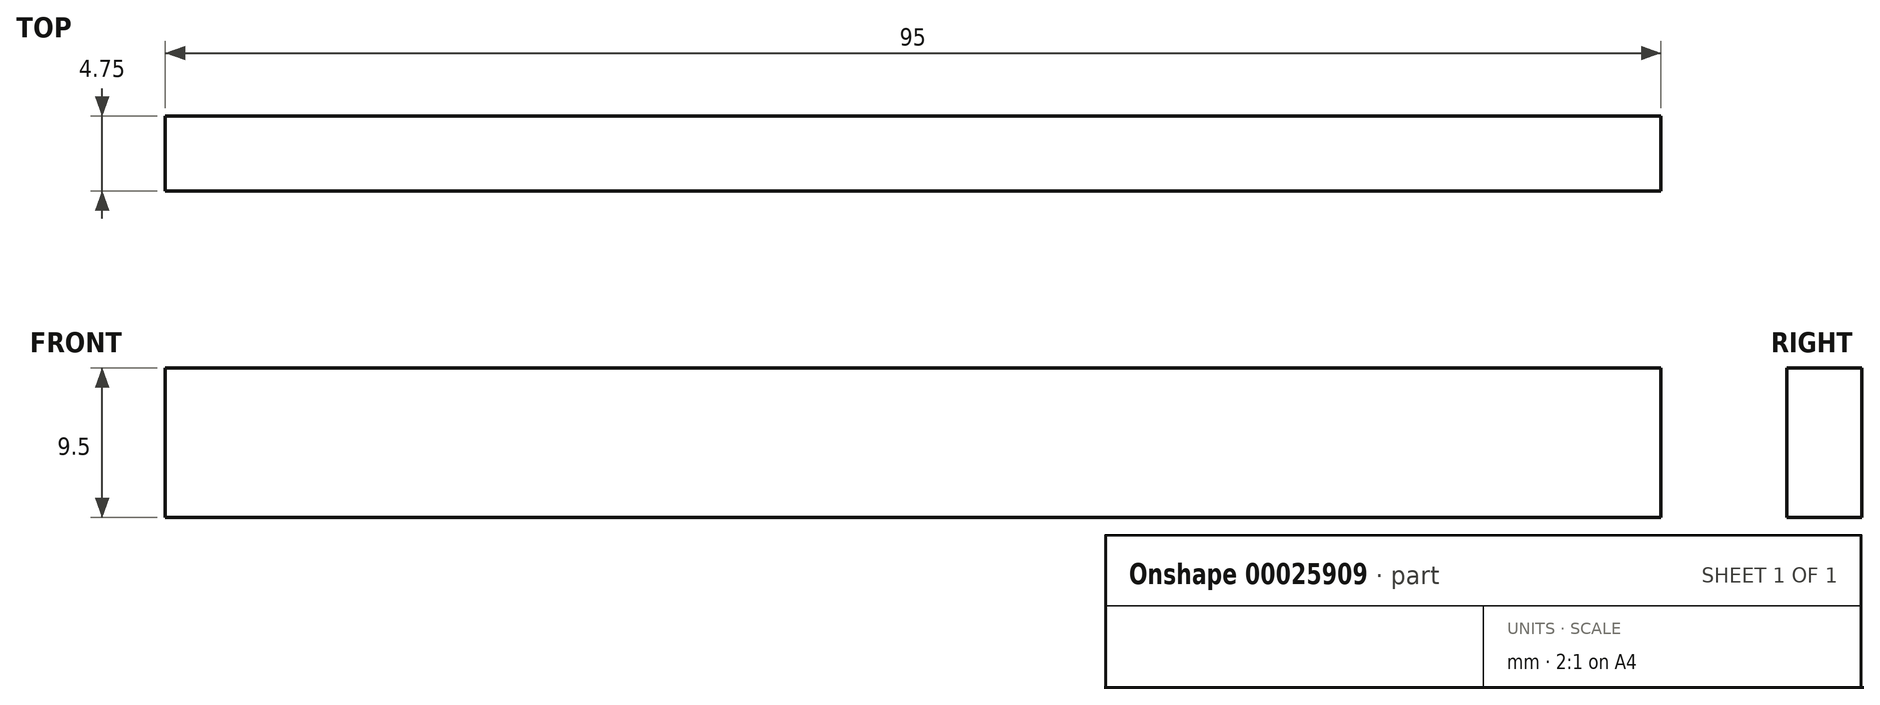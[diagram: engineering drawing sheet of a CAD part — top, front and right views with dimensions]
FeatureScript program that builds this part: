
annotation { "Feature Type Name" : "Feature", "Feature Type Description" : "" }
export const myFeature = defineFeature(function(context is Context, id is Id, definition is map)
    precondition{}
    {
        {
            var Q0;
            Q0=qCreatedBy(makeId("Front.planeOp"),FACE);
            var sketch = newSketch(context, id + "F0", { "sketchPlane" : qUnion([Q0])});
            skLineSegment(sketch, "E0.bottom", {"start": v(0, 0) * mm, "end": v(95, 0) * mm});
            skLineSegment(sketch, "E0.top", {"start": v(0, 9.5) * mm, "end": v(95, 9.5) * mm});
            skLineSegment(sketch, "E0.left", {"start": v(0, 0) * mm, "end": v(0, 9.5) * mm});
            skLineSegment(sketch, "E0.right", {"start": v(95, 0) * mm, "end": v(95, 9.5) * mm});
            skSolve(sketch);
        }
        {
            var Q0;
            Q0=makeQuery(id+"F0.imprint","IMPRINT",FACE,{"disambiguationData":[TD([[makeQuery(id+"F0.imprint","IMPRINT",EDGE,{"derivedFrom":sQuery(id+"F0.wireOp",EDGE,"E0.bottom")}),1.0]])]});
            extrude(context, id + "F1", {"entities" : qUnion([Q0]), "depth" : 4.75 * mm});
        }
    });
